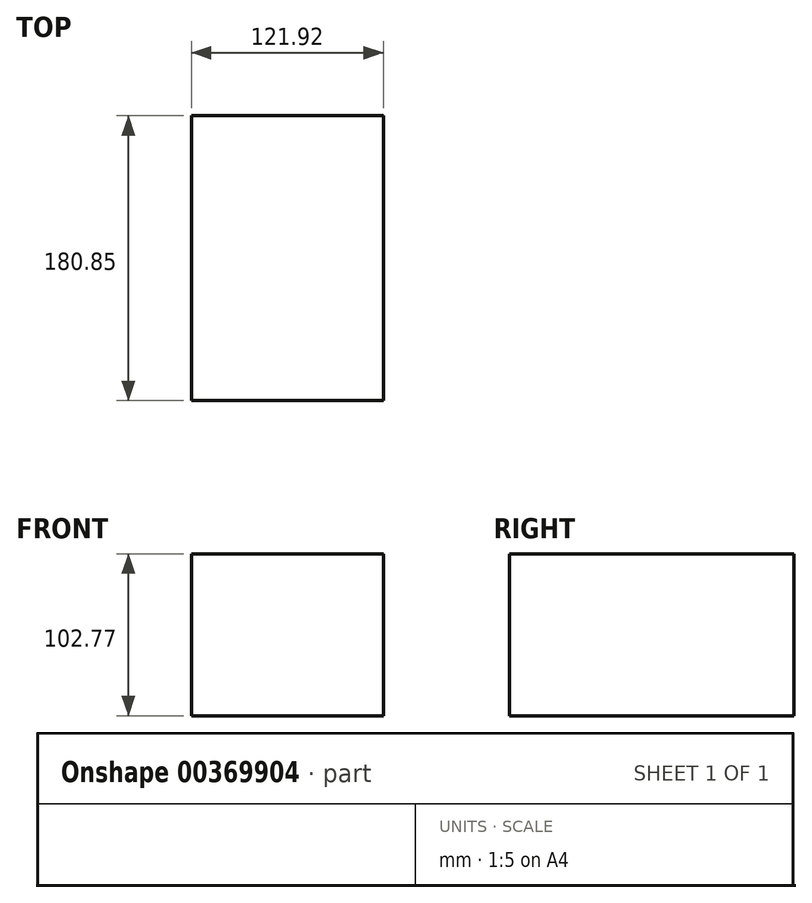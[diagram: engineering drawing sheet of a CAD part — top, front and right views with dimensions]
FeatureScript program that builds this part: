
annotation { "Feature Type Name" : "Feature", "Feature Type Description" : "" }
export const myFeature = defineFeature(function(context is Context, id is Id, definition is map)
    precondition{}
    {
        {
            var Q0;
            Q0=qCreatedBy(makeId("Front.planeOp"),FACE);
            var sketch = newSketch(context, id + "F0", { "sketchPlane" : qUnion([Q0])});
            skLineSegment(sketch, "E0", {"start": v(-144.5, 74.06) * mm, "end": v(-144.5, -28.71) * mm});
            skSolve(sketch);
        }
        {
            var Q0;
            Q0=sQuery(id+"F0.wireOp",EDGE,"E0");
            extrude(context, id + "F1", {"bodyType" : ToolBodyType.SURFACE, "surfaceEntities" : qUnion([Q0]), "depth" : 180.85 * mm});
        }
        {
            var Q0;
            Q0=makeQuery(id+"F1.opExtrude","SWEPT_FACE",FACE,{"disambiguationData":[OSD([sQuery(id+"F0.wireOp",EDGE,"E0")])]});
            extrude(context, id + "F2", {"entities" : qUnion([Q0]), "depth" : 121.92 * mm});
        }
    });
